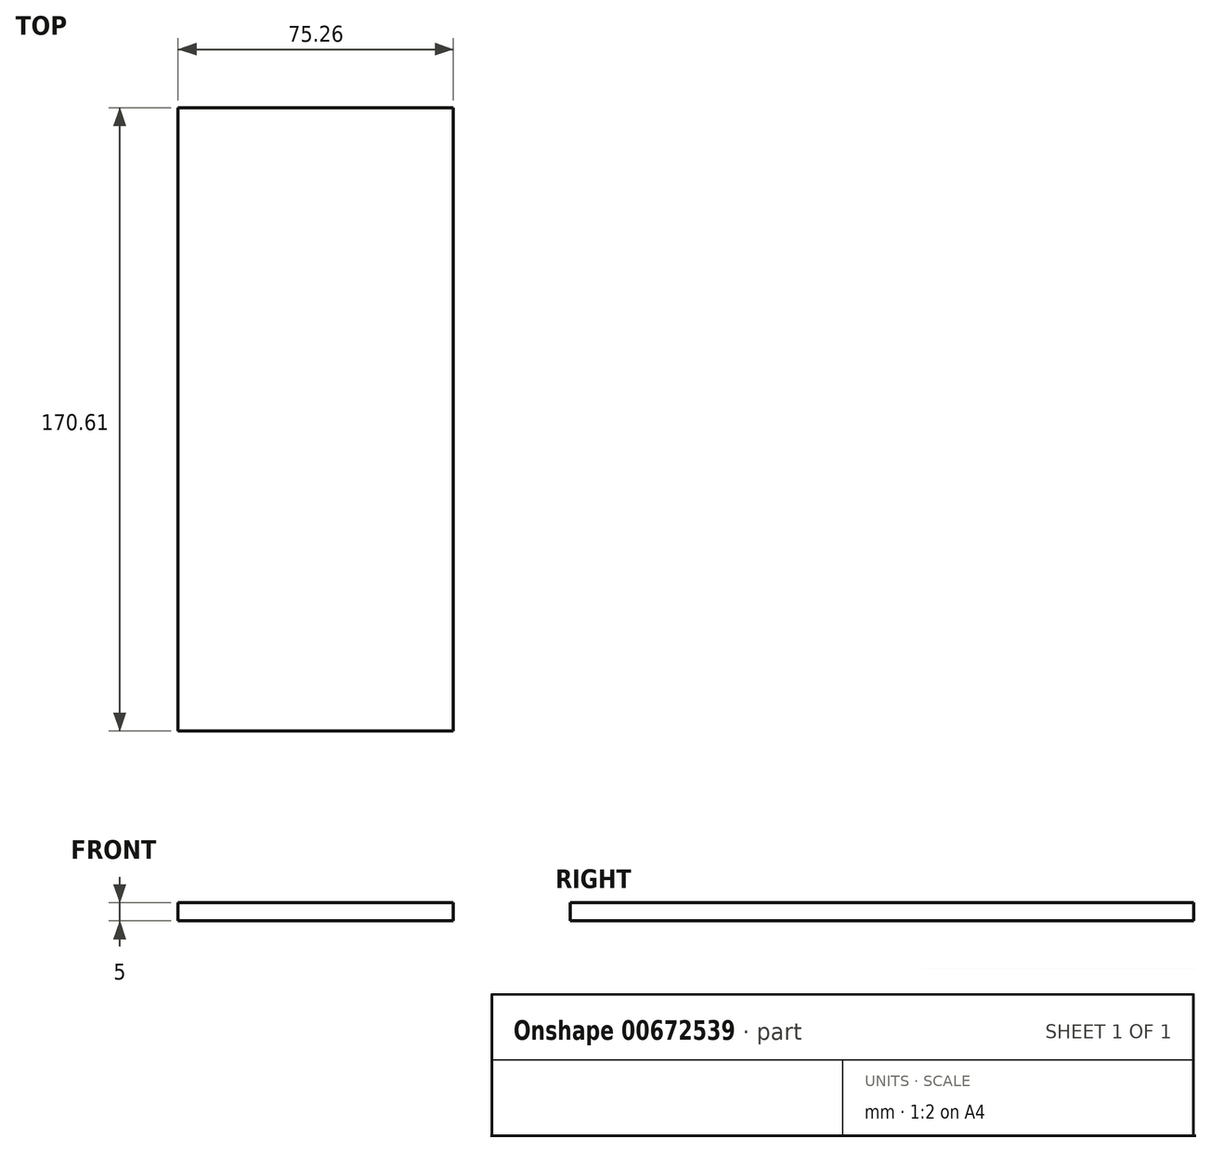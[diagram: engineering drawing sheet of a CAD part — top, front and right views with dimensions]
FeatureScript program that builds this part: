
annotation { "Feature Type Name" : "Feature", "Feature Type Description" : "" }
export const myFeature = defineFeature(function(context is Context, id is Id, definition is map)
    precondition{}
    {
        {
            var Q0;
            Q0=qCreatedBy(makeId("Top.planeOp"),FACE);
            var sketch = newSketch(context, id + "F0", { "sketchPlane" : qUnion([Q0])});
            skLineSegment(sketch, "E0.bottom", {"start": v(-33.23, 29.74) * mm, "end": v(42.03, 29.74) * mm});
            skLineSegment(sketch, "E0.top", {"start": v(-33.23, -61.24) * mm, "end": v(42.03, -61.24) * mm});
            skLineSegment(sketch, "E0.left", {"start": v(-33.23, 29.74) * mm, "end": v(-33.23, -61.24) * mm});
            skLineSegment(sketch, "E0.right", {"start": v(42.03, 29.74) * mm, "end": v(42.03, -61.24) * mm});
            skLineSegment(sketch, "E1.top", {"start": v(-33.23, -107.4) * mm, "end": v(42.03, -107.4) * mm});
            skLineSegment(sketch, "E1.left", {"start": v(-33.23, -61.24) * mm, "end": v(-33.23, -107.4) * mm});
            skLineSegment(sketch, "E1.right", {"start": v(42.03, -61.24) * mm, "end": v(42.03, -107.4) * mm});
            skLineSegment(sketch, "E2.top", {"start": v(-33.23, 63.22) * mm, "end": v(42.03, 63.22) * mm});
            skLineSegment(sketch, "E2.left", {"start": v(-33.23, 29.74) * mm, "end": v(-33.23, 63.22) * mm});
            skLineSegment(sketch, "E2.right", {"start": v(42.03, 29.74) * mm, "end": v(42.03, 63.22) * mm});
            skSolve(sketch);
        }
        {
            var Q0;
            Q0 = qSketchRegion(id + "F0", true);
            extrude(context, id + "F1", {"entities" : qUnion([Q0]), "depth" : 5 * mm, "offsetDistance" : 25 * mm});
        }
    });
